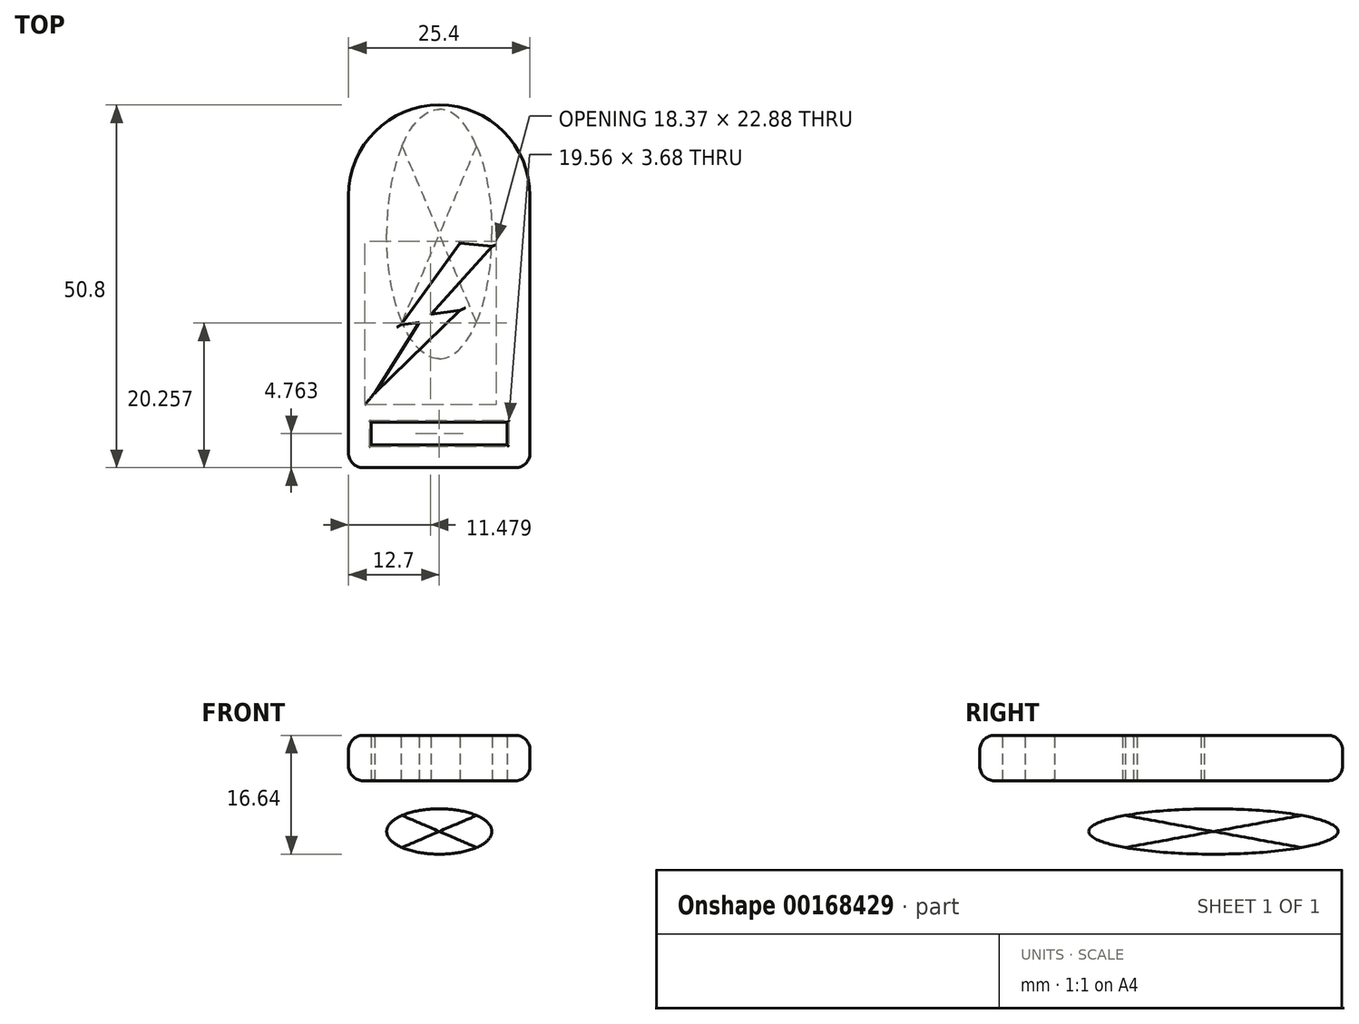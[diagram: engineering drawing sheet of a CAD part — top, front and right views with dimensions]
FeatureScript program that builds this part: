
annotation { "Feature Type Name" : "Feature", "Feature Type Description" : "" }
export const myFeature = defineFeature(function(context is Context, id is Id, definition is map)
    precondition{}
    {
        {
            var Q0;
            Q0=qCreatedBy(makeId("Top.planeOp"),FACE);
            var sketch = newSketch(context, id + "F0", { "sketchPlane" : qUnion([Q0])});
            skArc(sketch, "E0", {"start": v(12.7, 0) * mm, "mid": v(0, 12.7) * mm, "end": v(-12.7, 0) * mm});
            skLineSegment(sketch, "E1.top", {"start": v(-12.7, -38.1) * mm, "end": v(12.7, -38.1) * mm});
            skLineSegment(sketch, "E1.left", {"start": v(-12.7, 0) * mm, "end": v(-12.7, -38.1) * mm});
            skLineSegment(sketch, "E1.right", {"start": v(12.7, 0) * mm, "end": v(12.7, -38.1) * mm});
            skLineSegment(sketch, "E2", {"start": v(-12.7, -34.93) * mm, "end": v(-9.52, -34.93) * mm, "construction": true});
            skLineSegment(sketch, "E3", {"start": v(-9.53, -34.93) * mm, "end": v(-9.53, -38.1) * mm, "construction": true});
            skLineSegment(sketch, "E4.bottom", {"start": v(-9.52, -34.93) * mm, "end": v(9.53, -34.93) * mm});
            skLineSegment(sketch, "E4.top", {"start": v(-9.52, -31.75) * mm, "end": v(9.53, -31.75) * mm});
            skLineSegment(sketch, "E4.left", {"start": v(-9.52, -34.93) * mm, "end": v(-9.52, -31.75) * mm});
            skLineSegment(sketch, "E4.right", {"start": v(9.53, -34.93) * mm, "end": v(9.53, -31.75) * mm});
            skCircle(sketch, "E5", {"center": v(0, 0) * mm, "radius": 4.76 * mm});
            skLineSegment(sketch, "E6", {"start": v(-9.07, -27.64) * mm, "end": v(2.92, -16.06) * mm});
            skLineSegment(sketch, "E7", {"start": v(2.92, -16.06) * mm, "end": v(-1.2, -16.61) * mm});
            skLineSegment(sketch, "E8", {"start": v(-1.2, -16.61) * mm, "end": v(7.44, -7.09) * mm});
            skLineSegment(sketch, "E9", {"start": v(7.44, -7.09) * mm, "end": v(2.92, -6.67) * mm});
            skLineSegment(sketch, "E10", {"start": v(2.92, -6.67) * mm, "end": v(-5.35, -18.09) * mm});
            skLineSegment(sketch, "E11", {"start": v(-5.35, -18.09) * mm, "end": v(-2.83, -17.75) * mm});
            skLineSegment(sketch, "E12", {"start": v(-2.83, -17.75) * mm, "end": v(-9.07, -27.64) * mm});
            skSolve(sketch);
        }
        {
            var Q0;
            Q0=makeQuery(id+"F0.imprint","IMPRINT",FACE,{"disambiguationData":[TD([[makeQuery(id+"F0.imprint","IMPRINT",EDGE,{"derivedFrom":sQuery(id+"F0.wireOp",EDGE,"E0")}),1.0]])]});
            var Q1;
            Q1=makeQuery(id+"F0.imprint","IMPRINT",FACE,{"disambiguationData":[TD([[makeQuery(id+"F0.imprint","IMPRINT",EDGE,{"derivedFrom":sQuery(id+"F0.wireOp",EDGE,"E5")}),1.0]])]});
            extrude(context, id + "F1", {"entities" : qUnion([Q0, Q1]), "depth" : 6.35 * mm});
        }
        {
            var Q0;
            Q0=makeQuery(id+"F1.opExtrude","CAP_EDGE",EDGE,{"disambiguationData":[OSD([sQuery(id+"F0.wireOp",EDGE,"E1.left")])],"isStart":false});
            var Q1;
            Q1=makeQuery(id+"F1.opExtrude","CAP_EDGE",EDGE,{"disambiguationData":[OSD([sQuery(id+"F0.wireOp",EDGE,"E1.top")])],"isStart":false});
            var Q2;
            Q2=makeQuery(id+"F1.opExtrude","CAP_EDGE",EDGE,{"disambiguationData":[OSD([sQuery(id+"F0.wireOp",EDGE,"E1.top")])],"isStart":true});
            var Q3;
            Q3=makeQuery(id+"F1.opExtrude","SWEPT_EDGE",EDGE,{"disambiguationData":[OSD([sQuery(id+"F0.wireOp",EDGE,"E1.top"),sQuery(id+"F0.wireOp",EDGE,"E1.right")])]});
            var Q4;
            Q4=makeQuery(id+"F1.opExtrude","SWEPT_EDGE",EDGE,{"disambiguationData":[OSD([sQuery(id+"F0.wireOp",EDGE,"E1.top"),sQuery(id+"F0.wireOp",EDGE,"E1.left")])]});
            var Q5;
            Q5=makeQuery(id+"F1.opExtrude","CAP_EDGE",EDGE,{"disambiguationData":[OSD([sQuery(id+"F0.wireOp",EDGE,"E1.left")])],"isStart":true});
            fillet(context, id + "F2", {"entities" : qUnion([Q0, Q1, Q2, Q3, Q4, Q5]), "radius" : 2.03 * mm, "tangentPropagation" : true, "allowEdgeOverflow" : false});
        }
        {
            var Q0;
            Q0=makeQuery(id+"F1.opExtrude","CAP_EDGE",EDGE,{"disambiguationData":[OSD([sQuery(id+"F0.wireOp",EDGE,"E4.top")])],"isStart":false});
            var Q1;
            Q1=makeQuery(id+"F1.opExtrude","CAP_EDGE",EDGE,{"disambiguationData":[OSD([sQuery(id+"F0.wireOp",EDGE,"E4.bottom")])],"isStart":false});
            var Q2;
            Q2=makeQuery(id+"F1.opExtrude","CAP_EDGE",EDGE,{"disambiguationData":[OSD([sQuery(id+"F0.wireOp",EDGE,"E4.left")])],"isStart":false});
            var Q3;
            Q3=makeQuery(id+"F1.opExtrude","CAP_EDGE",EDGE,{"disambiguationData":[OSD([sQuery(id+"F0.wireOp",EDGE,"E4.right")])],"isStart":false});
            var Q4;
            Q4=makeQuery(id+"F1.opExtrude","CAP_EDGE",EDGE,{"disambiguationData":[OSD([sQuery(id+"F0.wireOp",EDGE,"E4.left")])],"isStart":true});
            var Q5;
            Q5=makeQuery(id+"F1.opExtrude","CAP_EDGE",EDGE,{"disambiguationData":[OSD([sQuery(id+"F0.wireOp",EDGE,"E4.top")])],"isStart":true});
            var Q6;
            Q6=makeQuery(id+"F1.opExtrude","CAP_EDGE",EDGE,{"disambiguationData":[OSD([sQuery(id+"F0.wireOp",EDGE,"E4.bottom")])],"isStart":true});
            var Q7;
            Q7=makeQuery(id+"F1.opExtrude","CAP_EDGE",EDGE,{"disambiguationData":[OSD([sQuery(id+"F0.wireOp",EDGE,"E4.right")])],"isStart":true});
            var Q8;
            Q8=makeQuery(id+"F1.opExtrude","CAP_EDGE",EDGE,{"disambiguationData":[OSD([sQuery(id+"F0.wireOp",EDGE,"E12")])],"isStart":true});
            var Q9;
            Q9=makeQuery(id+"F1.opExtrude","CAP_EDGE",EDGE,{"disambiguationData":[OSD([sQuery(id+"F0.wireOp",EDGE,"E10")])],"isStart":true});
            var Q10;
            Q10=makeQuery(id+"F1.opExtrude","CAP_EDGE",EDGE,{"disambiguationData":[OSD([sQuery(id+"F0.wireOp",EDGE,"E11")])],"isStart":true});
            var Q11;
            Q11=makeQuery(id+"F1.opExtrude","CAP_EDGE",EDGE,{"disambiguationData":[OSD([sQuery(id+"F0.wireOp",EDGE,"E8")])],"isStart":true});
            var Q12;
            Q12=makeQuery(id+"F1.opExtrude","CAP_EDGE",EDGE,{"disambiguationData":[OSD([sQuery(id+"F0.wireOp",EDGE,"E7")])],"isStart":true});
            var Q13;
            Q13=makeQuery(id+"F1.opExtrude","CAP_EDGE",EDGE,{"disambiguationData":[OSD([sQuery(id+"F0.wireOp",EDGE,"E6")])],"isStart":true});
            var Q14;
            Q14=makeQuery(id+"F1.opExtrude","CAP_EDGE",EDGE,{"disambiguationData":[OSD([sQuery(id+"F0.wireOp",EDGE,"E9")])],"isStart":true});
            var Q15;
            Q15=makeQuery(id+"F1.opExtrude","CAP_EDGE",EDGE,{"disambiguationData":[OSD([sQuery(id+"F0.wireOp",EDGE,"E9")])],"isStart":false});
            var Q16;
            Q16=makeQuery(id+"F1.opExtrude","CAP_EDGE",EDGE,{"disambiguationData":[OSD([sQuery(id+"F0.wireOp",EDGE,"E8")])],"isStart":false});
            var Q17;
            Q17=makeQuery(id+"F1.opExtrude","CAP_EDGE",EDGE,{"disambiguationData":[OSD([sQuery(id+"F0.wireOp",EDGE,"E10")])],"isStart":false});
            var Q18;
            Q18=makeQuery(id+"F1.opExtrude","CAP_EDGE",EDGE,{"disambiguationData":[OSD([sQuery(id+"F0.wireOp",EDGE,"E6")])],"isStart":false});
            var Q19;
            Q19=makeQuery(id+"F1.opExtrude","CAP_EDGE",EDGE,{"disambiguationData":[OSD([sQuery(id+"F0.wireOp",EDGE,"E12")])],"isStart":false});
            var Q20;
            Q20=makeQuery(id+"F1.opExtrude","CAP_EDGE",EDGE,{"disambiguationData":[OSD([sQuery(id+"F0.wireOp",EDGE,"E7")])],"isStart":false});
            var Q21;
            Q21=makeQuery(id+"F1.opExtrude","CAP_EDGE",EDGE,{"disambiguationData":[OSD([sQuery(id+"F0.wireOp",EDGE,"E11")])],"isStart":false});
            fillet(context, id + "F3", {"entities" : qUnion([Q0, Q1, Q2, Q3, Q4, Q5, Q6, Q7, Q8, Q9, Q10, Q11, Q12, Q13, Q14, Q15, Q16, Q17, Q18, Q19, Q20, Q21]), "radius" : 0.25 * mm, "tangentPropagation" : true, "allowEdgeOverflow" : false});
        }
        {
            var Q0;
            Q0=qCreatedBy(makeId("Top.planeOp"),FACE);
            cPlane(context, id + "F4", {"entities" : qUnion([Q0]), "cplaneType" : CPlaneType.OFFSET, "offset" : 7.11 * mm, "oppositeDirection" : true, "width" : 152.4 * mm, "height" : 152.4 * mm});
        }
        {
            var Q0;
            Q0=qCreatedBy(makeId("Front.planeOp"),FACE);
            cPlane(context, id + "F5", {"entities" : qUnion([Q0]), "cplaneType" : CPlaneType.OFFSET, "offset" : 5.38 * mm, "width" : 152.4 * mm, "height" : 152.4 * mm});
        }
        {
            var Q0;
            Q0=qCreatedBy(id+"F4.planeOp",FACE);
            var sketch = newSketch(context, id + "F6", { "sketchPlane" : qUnion([Q0])});
            skPoint(sketch, "E13", {"position": v(0, -5.38) * mm});
            skSolve(sketch);
        }
        {
            var Q0;
            Q0=qCreatedBy(id+"F4.planeOp",FACE);
            var sketch = newSketch(context, id + "F7", { "sketchPlane" : qUnion([Q0])});
            skEllipse(sketch, "E14", {"center": v(0, -5.38) * mm, "majorRadius": 17.46 * mm, "minorRadius": 7.37 * mm, "majorAxis": v(0, 1)});
            skSolve(sketch);
        }
        {
            var Q0;
            Q0=qCreatedBy(id+"F5.planeOp",FACE);
            var sketch = newSketch(context, id + "F8", { "sketchPlane" : qUnion([Q0])});
            skEllipse(sketch, "E15", {"center": v(0, -7.11) * mm, "majorRadius": 7.37 * mm, "minorRadius": 3.18 * mm, "majorAxis": v(1, 0)});
            skSolve(sketch);
        }
        {
            var Q0;
            Q0=qCreatedBy(makeId("Right.planeOp"),FACE);
            var sketch = newSketch(context, id + "F9", { "sketchPlane" : qUnion([Q0])});
            skEllipse(sketch, "E16", {"center": v(-5.38, -7.11) * mm, "majorRadius": 17.46 * mm, "minorRadius": 3.18 * mm, "majorAxis": v(-1, 0)});
            skSolve(sketch);
        }
        {
            var Q0;
            Q0 = qSketchRegion(id + "F7", true);
            var Q1;
            Q1=sQuery(id+"F7.wireOp",EDGE,"E14");
            extrude(context, id + "F10", {"entities" : qUnion([Q0]), "surfaceEntities" : qUnion([Q1]), "endBound" : BoundingType.SYMMETRIC, "depth" : 6.35 * mm});
        }
        {
            var Q0;
            Q0 = qSketchRegion(id + "F8", true);
            extrude(context, id + "F11", {"entities" : qUnion([Q0]), "endBound" : BoundingType.SYMMETRIC, "depth" : 34.92 * mm});
        }
        {
            var Q0;
            Q0 = qSketchRegion(id + "F9", true);
            extrude(context, id + "F12", {"entities" : qUnion([Q0]), "endBound" : BoundingType.SYMMETRIC, "depth" : 14.73 * mm});
        }
        {
            var Q0;
            Q0=makeQuery(id+"F11.opExtrude","SWEPT_BODY",BODY,{"disambiguationData":[OSD([sQuery(id+"F8.wireOp",EDGE,"E15")])]});
            var Q1;
            Q1=makeQuery(id+"F12.opExtrude","SWEPT_BODY",BODY,{"disambiguationData":[OSD([sQuery(id+"F9.wireOp",EDGE,"E16")])]});
            var Q2;
            Q2=makeQuery(id+"F10.opExtrude","SWEPT_BODY",BODY,{"disambiguationData":[OSD([sQuery(id+"F7.wireOp",EDGE,"E14")])]});
            booleanBodies(context, id + "F13", {"operationType" : BooleanOperationType.INTERSECTION, "tools" : qUnion([Q0, Q1, Q2])});
        }
    });
